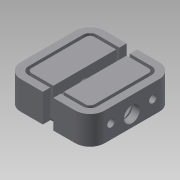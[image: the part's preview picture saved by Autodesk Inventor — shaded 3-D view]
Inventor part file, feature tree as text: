
AUTODESK INVENTOR PART (.ipt)
format: ipt  version: 2015 SP1 (Build 190203100, 203)  size: 389,120 bytes
history: native  units: mm
features: extrude x16, sketch x11, projected_geometry x7, mirror x4, fillet x2, plane x1
ambient origin geometry x8: Origin, YZ Plane, XZ Plane, XY Plane, X Axis, Y Axis, Z Axis, Center Point
bodies: Solid1 (feature_tree)
feature tree (41):
  sketch  "Sketch1"  dims[d0=30.0mm d1=30.0mm]
  extrude  "Extrusion1"  Depth=30.0mm
  extrude  "Extrusion2"  Depth=30.0mm TaperAngle=0.0deg
  extrude  "Extrusion3"  Depth=10.0mm
  sketch  "Sketch2"  dims[d2=3.0mm d3=0.0mm d4=30.0mm d5=0.0mm]
  extrude  "Extrusion6"  Depth=3.5mm
  extrude  "Extrusion7"  Depth=13.5mm TaperAngle=0.0deg
  extrude  "Extrusion8"  Depth=1.5mm
  extrude  "Extrusion9"  Depth=2.0mm
  fillet  "Fillet1"  Radius=2.0mm
  fillet  "Fillet2"  Radius=9.5mm
  plane  "Work Plane1"
  mirror  "Mirror3"
  mirror  "Mirror4"
  extrude  "Extrusion11"  Depth=1.5mm
  extrude  "Extrusion15"  Depth=3.5mm
  extrude  "Extrusion16"  Depth=5.5mm
  mirror  "Mirror7"
  extrude  "Extrusion17"  Depth=8.0mm TaperAngle=0.0deg
  extrude  "Extrusion18"  Depth=13.0mm
  mirror  "Mirror8"
  extrude  "Extrusion19"  Depth=2.0mm TaperAngle=0.0deg
  extrude  "Extrusion20"  Depth=3.5mm
  extrude  "Extrusion21"  Depth=2.0mm TaperAngle=0.0deg
  extrude  "Extrusion22"  Depth=8.0mm TaperAngle=0.0deg
  sketch  "Sketch6"  dims[d6=3.0mm d7=0.0mm d8=10.0mm]
  sketch  "Sketch10"  dims[d9=8.0mm d12=3.5mm]
  sketch  "Sketch11"  dims[d15=11.0mm d16=0.0mm d17=13.5mm d18=0.0mm]
  sketch  "Sketch12"  dims[d19=1.5mm d20=0.0mm d21=8.25mm]
  projected_geometry  "Projected Loop3"
  sketch  "Sketch13"  dims[d22=4.0mm d23=0.0mm d35=2.0mm d36=2.0mm d37=9.5mm]
  projected_geometry  "Projected Loop4"
  sketch  "Sketch15"  dims[d38=1.5mm d39=1.5mm]
  projected_geometry  "Projected Loop7"
  projected_geometry  "Projected Loop8"
  projected_geometry  "Projected Loop9"
  sketch  "Sketch16"  dims[d40=3.5mm d41=3.5mm]
  projected_geometry  "Projected Loop10"
  sketch  "Sketch18"  dims[d42=27.5mm d43=0.0mm d51=5.5mm]
  projected_geometry  "Projected Loop11"
  sketch  "Sketch19"  dims[d52=8.0mm d53=8.0mm d54=0.0mm d55=7.5mm d56=2.0mm d57=0.0mm d61=3.5mm d62=2.0mm d63=0.0mm d64=8.0mm d65=0.0mm d66=10.5mm d67=10.0mm d68=0.0mm d69=10.0mm d70=0.0mm d71=13.0mm d72=0.0mm d73=200.0mm d74=0.0mm]
